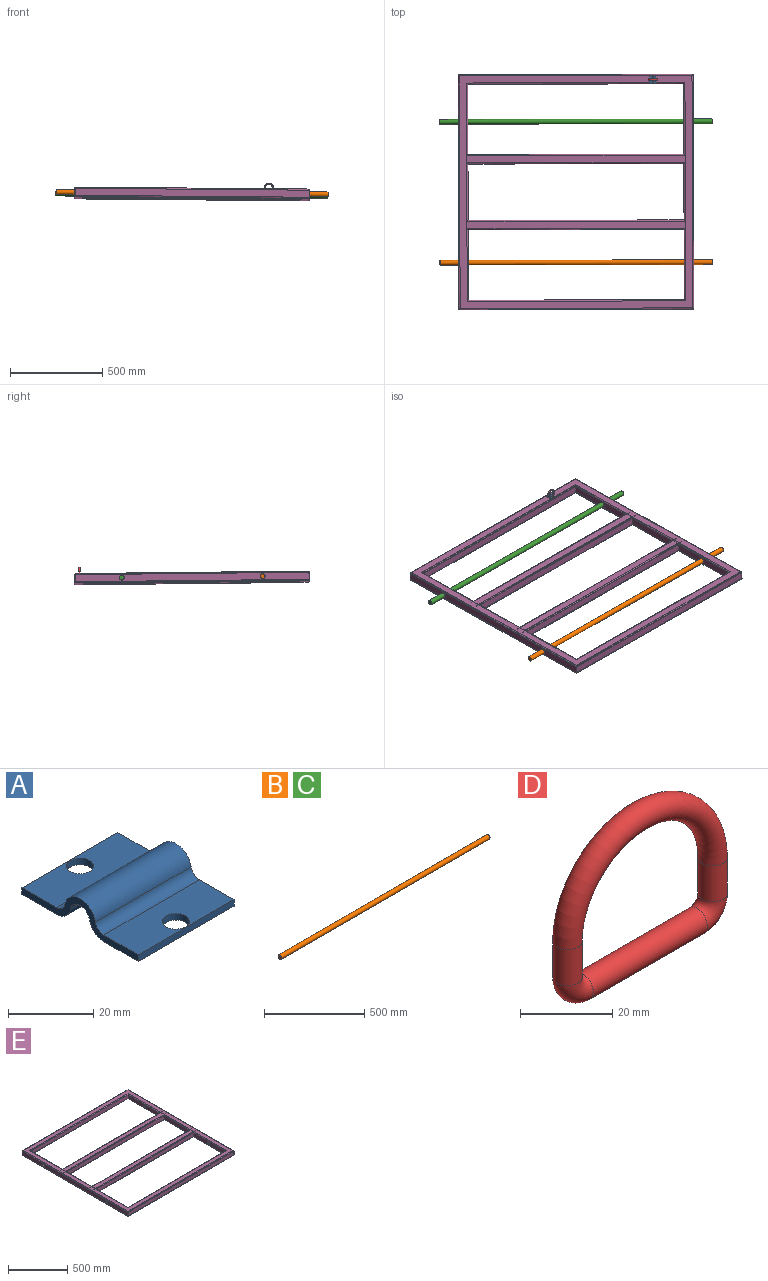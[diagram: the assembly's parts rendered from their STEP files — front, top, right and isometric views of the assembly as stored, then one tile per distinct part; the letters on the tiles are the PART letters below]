
ASSEMBLY  parts=5 mates=4
PART A: 16 faces, bbox 31.8x38.5x8.4 mm
  f0: plane 31.75x11.41mm, normal (0,0,1), area 330.5mm2, adj f1,f8,f12,f13,f14
  f1: cylinder r=3.17mm len=6.35mm, axis (0,0,-1), area 38mm2, adj f0,f7
  f2: cylinder r=3.17mm len=6.35mm, axis (0,0,-1), area 38mm2, adj f3,f11
  f3: plane 31.75x11.41mm, normal (0,0,-1), area 330.5mm2, adj f2,f4,f12,f13,f15
  f4: cylinder r=4.76mm len=31.75mm, axis (-1,0,0), area 208.5mm2, adj f3,f5,f12,f13
  f5: cylinder r=3.24mm len=31.75mm, axis (-1,0,0), area 283.6mm2, adj f4,f6,f12,f13
  f6: cylinder r=4.76mm len=31.75mm, axis (-1,0,0), area 208.5mm2, adj f5,f7,f12,f13
  f7: plane 31.75x11.41mm, normal (0,0,-1), area 330.5mm2, adj f1,f6,f12,f13,f14
  f8: cylinder r=2.86mm len=31.75mm, axis (-1,0,0), area 125.1mm2, adj f0,f9,f12,f13
  f9: cylinder r=5.14mm len=31.75mm, axis (-1,0,0), area 450.4mm2, adj f8,f10,f12,f13
  f10: cylinder r=2.86mm len=31.75mm, axis (-1,0,0), area 125.1mm2, adj f9,f11,f12,f13
  f11: plane 31.75x11.41mm, normal (0,0,1), area 330.5mm2, adj f2,f10,f12,f13,f15
  f12: plane 38.52x8.38mm, normal (1,0,0), area 85.5mm2, adj f0,f3,f4,f5,f6,f7,f8,f9
  f13: plane 38.52x8.38mm, normal (-1,0,0), area 85.5mm2, adj f0,f3,f4,f5,f6,f7,f8,f9
  f14: plane 31.75x1.91mm, normal (0,1,0), area 60.5mm2, adj f0,f7,f12,f13
  f15: plane 31.75x1.91mm, normal (0,-1,0), area 60.5mm2, adj f3,f11,f12,f13
PART B: 3 faces, bbox 1473.2x25.4x25.4 mm
  f0: cylinder r=12.7mm len=1473.2mm, axis (-1,0,0), area 117556.1mm2, adj f1,f2
  f1: plane 25.4x25.4mm, normal (1,0,0), area 506.7mm2, adj f0
  f2: plane 25.4x25.4mm, normal (-1,0,0), area 506.7mm2, adj f0
PART C: same geometry as B
PART D: 6 faces, bbox 55x6.4x45.6 mm
  f0: torus R=4.76mm, axis (0,1,0), area 149.2mm2, adj f3,f4
  f1: torus R=22.23mm, axis (0,1,0), area 1392.9mm2, adj f4,f5
  f2: torus R=4.76mm, axis (0,1,0), area 149.2mm2, adj f3,f5
  f3: cylinder r=3.17mm len=34.93mm, axis (1,0,0), area 696.7mm2, adj f0,f2
  f4: cylinder r=3.17mm len=9.53mm, axis (0,0,1), area 190mm2, adj f0,f1
  f5: cylinder r=3.17mm len=9.53mm, axis (0,0,-1), area 190mm2, adj f1,f2
PART E: 188 faces, bbox 1270x1270x50.8 mm
  f0: cylinder r=3.17mm len=44.45mm, axis (0,-1,0), area 210.2mm2, adj f4,f19,f36,f43
  f1: cylinder r=3.17mm len=388.2mm, axis (0,-1,0), area 1923.8mm2, adj f5,f19,f41,f48
  f2: cylinder r=3.17mm len=388.2mm, axis (0,-1,0), area 1923.8mm2, adj f7,f19,f22,f72
  f3: cylinder r=3.17mm len=306.5mm, axis (0,-1,0), area 1524.3mm2, adj f6,f19,f29,f34
  f4: plane 44.45x38.1mm, normal (1,0,0), area 1693.5mm2, adj f0,f9,f40,f47
  f5: plane 384.18x38.1mm, normal (1,0,0), area 14130.4mm2, adj f1,f12,f46,f49,f109
  f6: plane 304.8x38.1mm, normal (1,0,0), area 11612.9mm2, adj f3,f10,f33,f39
  f7: plane 384.18x38.1mm, normal (1,0,0), area 14130.4mm2, adj f2,f11,f26,f73,f156
  f8: plane 44.45x38.1mm, normal (1,0,0), area 1693.5mm2, adj f13,f14,f25,f32
  f9: cylinder r=3.17mm len=44.45mm, axis (0,-1,0), area 210.2mm2, adj f4,f15,f38,f45
  f10: cylinder r=3.17mm len=306.5mm, axis (0,-1,0), area 1524.3mm2, adj f6,f15,f31,f37
  f11: cylinder r=3.17mm len=388.2mm, axis (0,-1,0), area 1923.8mm2, adj f7,f15,f24,f74
  f12: cylinder r=3.17mm len=388.2mm, axis (0,-1,0), area 1923.8mm2, adj f5,f15,f44,f50
  f13: cylinder r=3.17mm len=44.45mm, axis (0,-1,0), area 210.2mm2, adj f8,f19,f21,f28
  f14: cylinder r=3.17mm len=44.45mm, axis (0,-1,0), area 210.2mm2, adj f8,f15,f23,f30
  f15: plane 1257.3x1257.3mm, normal (0,0,-1), area 184968mm2, adj f9,f10,f11,f12,f14,f16,f20,f23
  f16: cylinder r=3.17mm len=1263.65mm, axis (0,-1,0), area 6290.7mm2, adj f15,f17,f51,f75
  f17: plane 1263.65x38.1mm, normal (-1,0,0), area 47131.7mm2, adj f16,f18,f52,f76,f108,f157
  f18: cylinder r=3.17mm len=1263.65mm, axis (0,-1,0), area 6290.7mm2, adj f17,f19,f53,f77
  f19: plane 1257.3x1257.3mm, normal (0,0,1), area 184968mm2, adj f0,f1,f2,f3,f13,f18,f20,f21
  f20: plane 44.45x6.35mm, normal (1,0,0), area 143.7mm2, adj f15,f19,f21,f22,f23,f24,f25,f26
  f21: cylinder r=3.17mm len=22.23mm, axis (1,0,0), area 105.1mm2, adj f13,f19,f20,f25
  f22: cylinder r=6.35mm len=22.23mm, axis (1,0,0), area 71.5mm2, adj f2,f19,f20,f26
  f23: cylinder r=3.17mm len=22.23mm, axis (1,0,0), area 105.1mm2, adj f14,f15,f20,f25
  f24: cylinder r=6.35mm len=22.23mm, axis (1,0,0), area 71.5mm2, adj f11,f15,f20,f26
  f25: plane 38.1x22.23mm, normal (0,1,0), area 846.8mm2, adj f8,f20,f21,f23
  f26: plane 38.1x22.23mm, normal (0,-1,0), area 846.8mm2, adj f7,f20,f22,f24
  f27: plane 44.45x6.35mm, normal (1,0,0), area 143.7mm2, adj f15,f19,f28,f29,f30,f31,f32,f33
  f28: cylinder r=3.17mm len=22.23mm, axis (1,0,0), area 105.1mm2, adj f13,f19,f27,f32
  f29: cylinder r=6.35mm len=22.23mm, axis (1,0,0), area 71.5mm2, adj f3,f19,f27,f33
  f30: cylinder r=3.17mm len=22.23mm, axis (1,0,0), area 105.1mm2, adj f14,f15,f27,f32
  f31: cylinder r=6.35mm len=22.23mm, axis (1,0,0), area 71.5mm2, adj f10,f15,f27,f33
  f32: plane 38.1x22.23mm, normal (0,-1,0), area 846.8mm2, adj f8,f27,f28,f30
  f33: plane 38.1x22.23mm, normal (0,1,0), area 846.8mm2, adj f6,f27,f29,f31
  f34: cylinder r=6.35mm len=22.23mm, axis (1,0,0), area 71.5mm2, adj f3,f19,f35,f39
  f35: plane 44.45x6.35mm, normal (1,0,0), area 143.7mm2, adj f15,f19,f34,f36,f37,f38,f39,f40
  f36: cylinder r=3.17mm len=22.23mm, axis (1,0,0), area 105.1mm2, adj f0,f19,f35,f40
  f37: cylinder r=6.35mm len=22.23mm, axis (1,0,0), area 71.5mm2, adj f10,f15,f35,f39
  f38: cylinder r=3.17mm len=22.23mm, axis (1,0,0), area 105.1mm2, adj f9,f15,f35,f40
  f39: plane 38.1x22.23mm, normal (0,-1,0), area 846.8mm2, adj f6,f34,f35,f37
  f40: plane 38.1x22.23mm, normal (0,1,0), area 846.8mm2, adj f4,f35,f36,f38
  f41: cylinder r=6.35mm len=22.23mm, axis (1,0,0), area 71.5mm2, adj f1,f19,f42,f46
  f42: plane 44.45x6.35mm, normal (1,0,0), area 143.7mm2, adj f15,f19,f41,f43,f44,f45,f46,f47
  f43: cylinder r=3.17mm len=22.23mm, axis (1,0,0), area 105.1mm2, adj f0,f19,f42,f47
  f44: cylinder r=6.35mm len=22.23mm, axis (1,0,0), area 71.5mm2, adj f12,f15,f42,f46
  f45: cylinder r=3.17mm len=22.23mm, axis (1,0,0), area 105.1mm2, adj f9,f15,f42,f47
  f46: plane 38.1x22.23mm, normal (0,1,0), area 846.8mm2, adj f5,f41,f42,f44
  f47: plane 38.1x22.23mm, normal (0,-1,0), area 846.8mm2, adj f4,f42,f43,f45
  f48: cylinder r=3.17mm len=1181.1mm, axis (1,0,0), area 5870.4mm2, adj f1,f19,f49,f62
  f49: plane 1174.75x38.1mm, normal (0,1,0), area 44758mm2, adj f5,f48,f50,f63
  f50: cylinder r=3.17mm len=1181.1mm, axis (1,0,0), area 5870.4mm2, adj f12,f15,f49,f66
  f51: cylinder r=3.17mm len=1263.65mm, axis (1,0,0), area 6290.7mm2, adj f15,f16,f52,f69
  f52: plane 1263.65x38.1mm, normal (0,-1,0), area 48145.1mm2, adj f17,f51,f53,f70
  f53: cylinder r=3.17mm len=1263.65mm, axis (1,0,0), area 6290.7mm2, adj f18,f19,f52,f71
  f54: cylinder r=3.17mm len=388.2mm, axis (0,1,0), area 1923.8mm2, adj f19,f56,f72,f101
  f55: cylinder r=3.17mm len=306.5mm, axis (0,1,0), area 1524.3mm2, adj f19,f57,f90,f94
  f56: plane 384.18x38.1mm, normal (-1,0,0), area 14130.4mm2, adj f54,f59,f73,f105,f158
  f57: plane 304.8x38.1mm, normal (-1,0,0), area 11612.9mm2, adj f55,f60,f86,f98
  f58: plane 44.45x38.1mm, normal (-1,0,0), area 1693.5mm2, adj f61,f65,f97,f104
  f59: cylinder r=3.17mm len=388.2mm, axis (0,1,0), area 1923.8mm2, adj f15,f56,f74,f103
  f60: cylinder r=3.17mm len=306.5mm, axis (0,1,0), area 1524.3mm2, adj f15,f57,f91,f96
  f61: cylinder r=3.17mm len=44.45mm, axis (0,1,0), area 210.2mm2, adj f19,f58,f92,f99
  f62: cylinder r=3.17mm len=388.2mm, axis (0,1,0), area 1923.8mm2, adj f19,f48,f63,f80
  f63: plane 384.18x38.1mm, normal (-1,0,0), area 14130.4mm2, adj f49,f62,f66,f84,f107
  f64: plane 44.45x38.1mm, normal (-1,0,0), area 1693.5mm2, adj f67,f68,f83,f87
  f65: cylinder r=3.17mm len=44.45mm, axis (0,1,0), area 210.2mm2, adj f15,f58,f95,f102
  f66: cylinder r=3.17mm len=388.2mm, axis (0,1,0), area 1923.8mm2, adj f15,f50,f63,f82
  f67: cylinder r=3.17mm len=44.45mm, axis (0,1,0), area 210.2mm2, adj f19,f64,f78,f89
  f68: cylinder r=3.17mm len=44.45mm, axis (0,1,0), area 210.2mm2, adj f15,f64,f81,f85
  f69: cylinder r=3.17mm len=1263.65mm, axis (0,1,0), area 6290.7mm2, adj f15,f51,f70,f75
  f70: plane 1263.65x38.1mm, normal (1,0,0), area 47131.7mm2, adj f52,f69,f71,f76,f106,f159
  f71: cylinder r=3.17mm len=1263.65mm, axis (0,1,0), area 6290.7mm2, adj f19,f53,f70,f77
  f72: cylinder r=3.17mm len=1181.1mm, axis (-1,0,0), area 5870.4mm2, adj f2,f19,f54,f73
  f73: plane 1174.75x38.1mm, normal (0,-1,0), area 44758mm2, adj f7,f56,f72,f74
  f74: cylinder r=3.17mm len=1181.1mm, axis (-1,0,0), area 5870.4mm2, adj f11,f15,f59,f73
  f75: cylinder r=3.17mm len=1263.65mm, axis (-1,0,0), area 6290.7mm2, adj f15,f16,f69,f76
  f76: plane 1263.65x38.1mm, normal (0,1,0), area 48145.1mm2, adj f17,f70,f75,f77
  f77: cylinder r=3.17mm len=1263.65mm, axis (-1,0,0), area 6290.7mm2, adj f18,f19,f71,f76
  f78: cylinder r=3.17mm len=22.23mm, axis (1,0,0), area 105.1mm2, adj f19,f67,f79,f83
  f79: plane 44.45x6.35mm, normal (-1,0,0), area 143.7mm2, adj f15,f19,f78,f80,f81,f82,f83,f84
  f80: cylinder r=6.35mm len=22.23mm, axis (1,0,0), area 71.5mm2, adj f19,f62,f79,f84
  f81: cylinder r=3.17mm len=22.23mm, axis (1,0,0), area 105.1mm2, adj f15,f68,f79,f83
  f82: cylinder r=6.35mm len=22.23mm, axis (1,0,0), area 71.5mm2, adj f15,f66,f79,f84
  f83: plane 38.1x22.23mm, normal (0,-1,0), area 846.8mm2, adj f64,f78,f79,f81
  f84: plane 38.1x22.23mm, normal (0,1,0), area 846.8mm2, adj f63,f79,f80,f82
  f85: cylinder r=3.17mm len=22.23mm, axis (1,0,0), area 105.1mm2, adj f15,f68,f87,f88
  f86: plane 38.1x22.23mm, normal (0,-1,0), area 846.8mm2, adj f57,f88,f90,f91
  f87: plane 38.1x22.23mm, normal (0,1,0), area 846.8mm2, adj f64,f85,f88,f89
  f88: plane 44.45x6.35mm, normal (-1,0,0), area 143.7mm2, adj f15,f19,f85,f86,f87,f89,f90,f91
  f89: cylinder r=3.17mm len=22.23mm, axis (1,0,0), area 105.1mm2, adj f19,f67,f87,f88
  f90: cylinder r=6.35mm len=22.23mm, axis (1,0,0), area 71.5mm2, adj f19,f55,f86,f88
  f91: cylinder r=6.35mm len=22.23mm, axis (1,0,0), area 71.5mm2, adj f15,f60,f86,f88
  f92: cylinder r=3.17mm len=22.23mm, axis (1,0,0), area 105.1mm2, adj f19,f61,f93,f97
  f93: plane 44.45x6.35mm, normal (-1,0,0), area 143.7mm2, adj f15,f19,f92,f94,f95,f96,f97,f98
  f94: cylinder r=6.35mm len=22.23mm, axis (1,0,0), area 71.5mm2, adj f19,f55,f93,f98
  f95: cylinder r=3.17mm len=22.23mm, axis (1,0,0), area 105.1mm2, adj f15,f65,f93,f97
  f96: cylinder r=6.35mm len=22.23mm, axis (1,0,0), area 71.5mm2, adj f15,f60,f93,f98
  f97: plane 38.1x22.23mm, normal (0,-1,0), area 846.8mm2, adj f58,f92,f93,f95
  f98: plane 38.1x22.23mm, normal (0,1,0), area 846.8mm2, adj f57,f93,f94,f96
  f99: cylinder r=3.17mm len=22.23mm, axis (1,0,0), area 105.1mm2, adj f19,f61,f100,f104
  f100: plane 44.45x6.35mm, normal (-1,0,0), area 143.7mm2, adj f15,f19,f99,f101,f102,f103,f104,f105
  f101: cylinder r=6.35mm len=22.23mm, axis (1,0,0), area 71.5mm2, adj f19,f54,f100,f105
  f102: cylinder r=3.17mm len=22.23mm, axis (1,0,0), area 105.1mm2, adj f15,f65,f100,f104
  f103: cylinder r=6.35mm len=22.23mm, axis (1,0,0), area 71.5mm2, adj f15,f59,f100,f105
  f104: plane 38.1x22.23mm, normal (0,1,0), area 846.8mm2, adj f58,f99,f100,f102
  f105: plane 38.1x22.23mm, normal (0,-1,0), area 846.8mm2, adj f56,f100,f101,f103
  f106: cylinder r=12.7mm len=25.4mm, axis (1,0,0), area 253.4mm2, adj f70,f111
  f107: cylinder r=12.7mm len=25.4mm, axis (1,0,0), area 253.4mm2, adj f63,f113
  f108: cylinder r=12.7mm len=25.4mm, axis (1,0,0), area 253.4mm2, adj f17,f150
  f109: cylinder r=12.7mm len=25.4mm, axis (1,0,0), area 253.4mm2, adj f5,f148
  f110: cylinder r=6.35mm len=1270mm, axis (0,1,0), area 12621.8mm2, adj f111,f122,f123,f146
  f111: plane 1270x38.1mm, normal (-1,0,0), area 47373.6mm2, adj f106,f110,f112,f121,f124,f159
  f112: cylinder r=6.35mm len=1270mm, axis (0,1,0), area 12621.8mm2, adj f111,f120,f125,f147
  f113: plane 381x38.1mm, normal (1,0,0), area 14009.4mm2, adj f107,f116,f127,f137,f145
  f114: plane 381x38.1mm, normal (1,0,0), area 14009.4mm2, adj f116,f118,f136,f137,f158
  f115: plane 304.8x38.1mm, normal (1,0,0), area 11612.9mm2, adj f116,f135,f137,f144
  f116: cylinder r=6.35mm len=1181.1mm, axis (0,1,0), area 10779.1mm2, adj f113,f114,f115,f119,f126,f132,f133,f134
  f117: cylinder r=6.35mm len=1181.1mm, axis (-1,0,0), area 11700.4mm2, adj f118,f137,f146,f154
  f118: plane 1168.4x38.1mm, normal (0,1,0), area 44516mm2, adj f114,f117,f119,f153
  f119: cylinder r=6.35mm len=1181.1mm, axis (-1,0,0), area 11700.4mm2, adj f116,f118,f147,f152
  f120: cylinder r=6.35mm len=1270mm, axis (-1,0,0), area 12621.8mm2, adj f112,f121,f147,f149
  f121: plane 1270x38.1mm, normal (0,-1,0), area 48387mm2, adj f111,f120,f122,f150
  f122: cylinder r=6.35mm len=1270mm, axis (-1,0,0), area 12621.8mm2, adj f110,f121,f146,f151
  f123: cylinder r=6.35mm len=1270mm, axis (1,0,0), area 12621.8mm2, adj f110,f124,f146,f151
  f124: plane 1270x38.1mm, normal (0,1,0), area 48387mm2, adj f111,f123,f125,f150
  f125: cylinder r=6.35mm len=1270mm, axis (1,0,0), area 12621.8mm2, adj f112,f124,f147,f149
  f126: cylinder r=6.35mm len=1181.1mm, axis (1,0,0), area 11700.4mm2, adj f116,f127,f147,f152
  f127: plane 1168.4x38.1mm, normal (0,-1,0), area 44516mm2, adj f113,f126,f128,f148
  f128: cylinder r=6.35mm len=1181.1mm, axis (1,0,0), area 11700.4mm2, adj f127,f137,f146,f154
  f129: plane 1181.1x38.1mm, normal (0,0,-1), area 44999.9mm2, adj f130,f131,f137,f154
  f130: cylinder r=6.35mm len=1181.1mm, axis (1,0,0), area 11700.4mm2, adj f129,f135,f137,f154
  f131: cylinder r=6.35mm len=1181.1mm, axis (1,0,0), area 11700.4mm2, adj f129,f136,f137,f154
  f132: plane 1181.1x38.1mm, normal (0,0,1), area 44999.9mm2, adj f116,f133,f134,f152
  f133: cylinder r=6.35mm len=1181.1mm, axis (1,0,0), area 11700.4mm2, adj f116,f132,f136,f152
  f134: cylinder r=6.35mm len=1181.1mm, axis (1,0,0), area 11700.4mm2, adj f116,f132,f135,f152
  f135: plane 1168.4x38.1mm, normal (0,1,0), area 44516mm2, adj f115,f130,f134,f155
  f136: plane 1168.4x38.1mm, normal (0,-1,0), area 44516mm2, adj f114,f131,f133,f153
  f137: cylinder r=6.35mm len=1181.1mm, axis (0,1,0), area 10779.1mm2, adj f113,f114,f115,f117,f128,f129,f130,f131
  f138: plane 1181.1x38.1mm, normal (0,0,1), area 44999.9mm2, adj f116,f139,f140,f152
  f139: cylinder r=6.35mm len=1181.1mm, axis (1,0,0), area 11700.4mm2, adj f116,f138,f145,f152
  f140: cylinder r=6.35mm len=1181.1mm, axis (1,0,0), area 11700.4mm2, adj f116,f138,f144,f152
  f141: plane 1181.1x38.1mm, normal (0,0,-1), area 44999.9mm2, adj f137,f142,f143,f154
  f142: cylinder r=6.35mm len=1181.1mm, axis (1,0,0), area 11700.4mm2, adj f137,f141,f144,f154
  f143: cylinder r=6.35mm len=1181.1mm, axis (1,0,0), area 11700.4mm2, adj f137,f141,f145,f154
  f144: plane 1168.4x38.1mm, normal (0,-1,0), area 44516mm2, adj f115,f140,f142,f155
  f145: plane 1168.4x38.1mm, normal (0,1,0), area 44516mm2, adj f113,f139,f143,f148
  f146: plane 1257.3x1257.3mm, normal (0,0,-1), area 185806.1mm2, adj f110,f117,f122,f123,f128,f137,f151,f154
  f147: plane 1257.3x1257.3mm, normal (0,0,1), area 185806.1mm2, adj f112,f116,f119,f120,f125,f126,f149,f152
  f148: plane 381x38.1mm, normal (-1,0,0), area 14009.4mm2, adj f109,f127,f145,f152,f154
  f149: cylinder r=6.35mm len=1270mm, axis (0,-1,0), area 12621.8mm2, adj f120,f125,f147,f150
  f150: plane 1270x38.1mm, normal (1,0,0), area 47373.6mm2, adj f108,f121,f124,f149,f151,f157
  f151: cylinder r=6.35mm len=1270mm, axis (0,-1,0), area 12621.8mm2, adj f122,f123,f146,f150
  f152: cylinder r=6.35mm len=1181.1mm, axis (0,-1,0), area 10779.1mm2, adj f119,f126,f132,f133,f134,f138,f139,f140
  f153: plane 381x38.1mm, normal (-1,0,0), area 14009.4mm2, adj f118,f136,f152,f154,f156
  f154: cylinder r=6.35mm len=1181.1mm, axis (0,-1,0), area 10779.1mm2, adj f117,f128,f129,f130,f131,f141,f142,f143
  f155: plane 304.8x38.1mm, normal (-1,0,0), area 11612.9mm2, adj f135,f144,f152,f154
  f156: cylinder r=12.7mm len=25.4mm, axis (1,0,0), area 253.4mm2, adj f7,f153
  f157: cylinder r=12.7mm len=25.4mm, axis (1,0,0), area 253.4mm2, adj f17,f150
  f158: cylinder r=12.7mm len=25.4mm, axis (1,0,0), area 253.4mm2, adj f56,f114
  f159: cylinder r=12.7mm len=25.4mm, axis (1,0,0), area 253.4mm2, adj f70,f111
  f160: plane 44.45x38.1mm, normal (1,0,0), area 1693.5mm2, adj f161,f162,f169,f170
  f161: cylinder r=6.35mm len=44.45mm, axis (0,1,0), area 143.1mm2, adj f160,f163,f164,f165
  f162: cylinder r=6.35mm len=44.45mm, axis (0,1,0), area 143.1mm2, adj f160,f166,f167,f168
  f163: cylinder r=3.17mm len=1170.1mm, axis (1,0,0), area 5831.4mm2, adj f161,f165,f170,f172
  f164: cylinder r=3.17mm len=1170.1mm, axis (1,0,0), area 5831.4mm2, adj f161,f165,f169,f172
  f165: plane 1170.1x38.1mm, normal (0,0,1), area 44580.9mm2, adj f161,f163,f164,f172
  f166: cylinder r=3.17mm len=1170.1mm, axis (1,0,0), area 5831.4mm2, adj f162,f167,f169,f171
  f167: plane 1170.1x38.1mm, normal (0,0,-1), area 44580.9mm2, adj f162,f166,f168,f171
  f168: cylinder r=3.17mm len=1170.1mm, axis (1,0,0), area 5831.4mm2, adj f162,f167,f170,f171
  f169: plane 1168.4x38.1mm, normal (0,1,0), area 44516mm2, adj f160,f164,f166,f173
  f170: plane 1168.4x38.1mm, normal (0,-1,0), area 44516mm2, adj f160,f163,f168,f173
  f171: cylinder r=6.35mm len=44.45mm, axis (0,-1,0), area 143.1mm2, adj f166,f167,f168,f173
  f172: cylinder r=6.35mm len=44.45mm, axis (0,-1,0), area 143.1mm2, adj f163,f164,f165,f173
  f173: plane 44.45x38.1mm, normal (-1,0,0), area 1693.5mm2, adj f169,f170,f171,f172
  f174: plane 44.45x38.1mm, normal (1,0,0), area 1693.5mm2, adj f175,f176,f183,f184
  f175: cylinder r=6.35mm len=44.45mm, axis (0,1,0), area 143.1mm2, adj f174,f180,f181,f182
  f176: cylinder r=6.35mm len=44.45mm, axis (0,1,0), area 143.1mm2, adj f174,f177,f178,f179
  f177: plane 1170.1x38.1mm, normal (0,0,-1), area 44580.9mm2, adj f176,f178,f179,f186
  f178: cylinder r=3.17mm len=1170.1mm, axis (1,0,0), area 5831.4mm2, adj f176,f177,f183,f186
  f179: cylinder r=3.17mm len=1170.1mm, axis (1,0,0), area 5831.4mm2, adj f176,f177,f184,f186
  f180: cylinder r=3.17mm len=1170.1mm, axis (1,0,0), area 5831.4mm2, adj f175,f182,f183,f185
  f181: cylinder r=3.17mm len=1170.1mm, axis (1,0,0), area 5831.4mm2, adj f175,f182,f184,f185
  f182: plane 1170.1x38.1mm, normal (0,0,1), area 44580.9mm2, adj f175,f180,f181,f185
  f183: plane 1168.4x38.1mm, normal (0,-1,0), area 44516mm2, adj f174,f178,f180,f187
  f184: plane 1168.4x38.1mm, normal (0,1,0), area 44516mm2, adj f174,f179,f181,f187
  f185: cylinder r=6.35mm len=44.45mm, axis (0,-1,0), area 143.1mm2, adj f180,f181,f182,f187
  f186: cylinder r=6.35mm len=44.45mm, axis (0,-1,0), area 143.1mm2, adj f177,f178,f179,f187
  f187: plane 44.45x38.1mm, normal (-1,0,0), area 1693.5mm2, adj f183,f184,f185,f186
PLACE A rot(axis=(-0.78,0.61,0.15),0.8deg) t=(389.17,608.47,-266.94)mm
PLACE B rot(axis=(-0.78,0.61,0.15),0.8deg) t=(-762.29,-382.72,-275.61)mm
PLACE C rot(axis=(-0.78,0.61,0.15),0.8deg) t=(-763.92,379.23,-283.62)mm
PLACE D rot(axis=(0,0.97,0.24),0.5deg) t=(389.17,608.47,-266.94)mm
PLACE E rot(axis=(-0.78,0.61,0.15),0.8deg) t=(-26.53,-0.23,-285.73)mm
MATE revolute B.f0 <-> E.f156  axis (-1,0,0.01) through (-25.71,-381.21,-281.73)mm
MATE planar A.f7 <-> E.f132  axis (-0.01,-0.01,-1) through (389.11,621.77,-270.32)mm
MATE revolute C.f0 <-> E.f106  axis (-1,0,0.01) through (-27.35,380.75,-289.74)mm
MATE revolute D.f3 <-> A.f5  axis (1,0,-0.01) through (389.17,608.47,-266.94)mm
